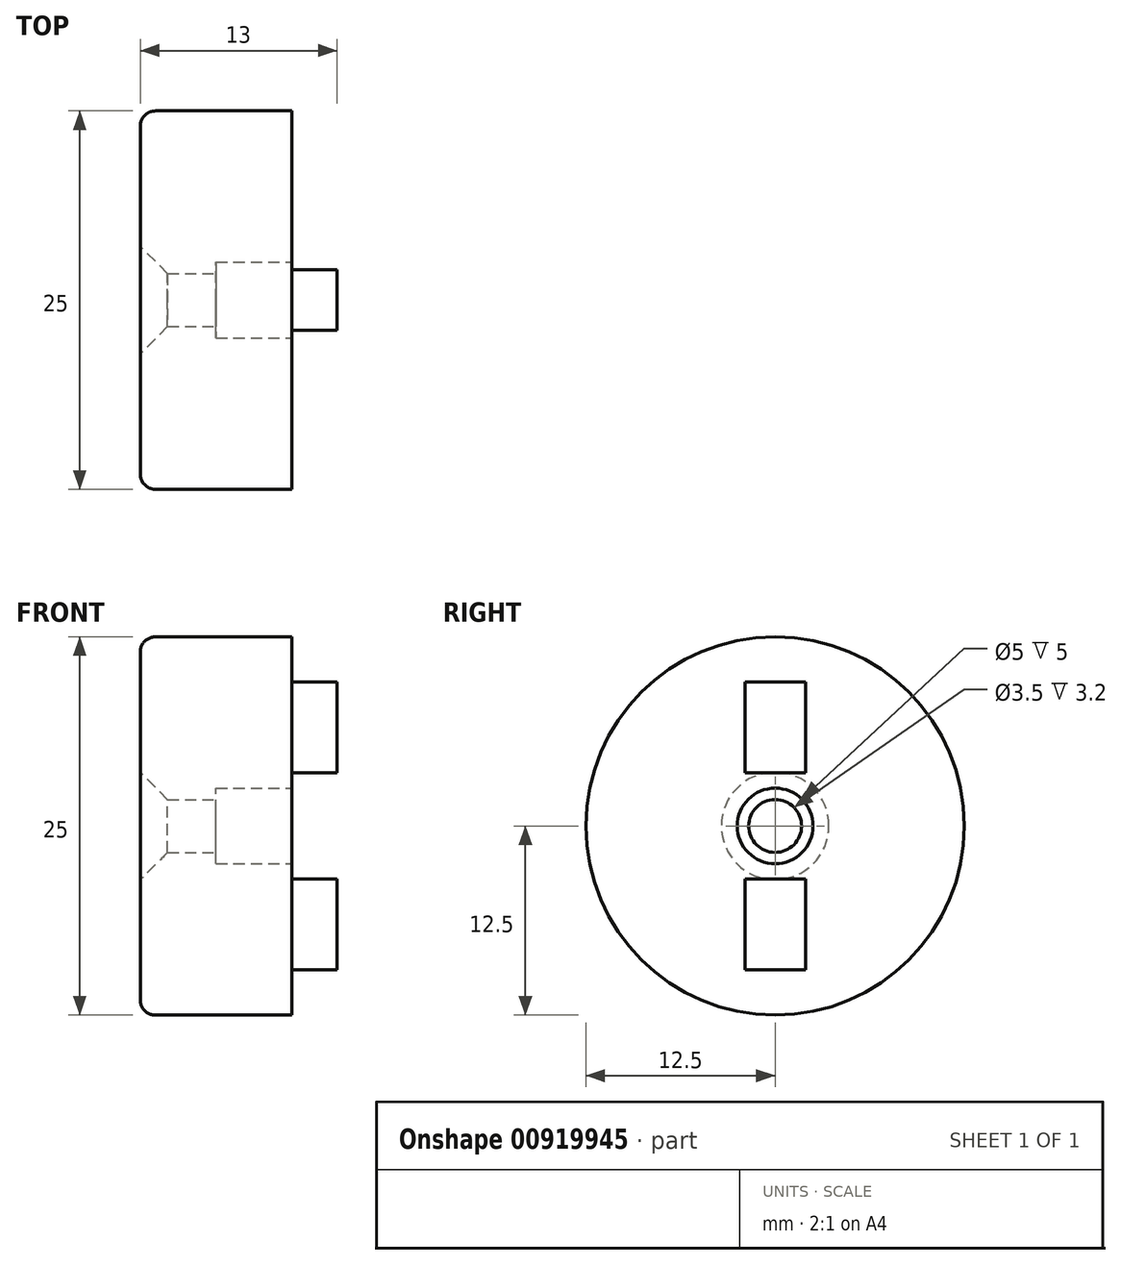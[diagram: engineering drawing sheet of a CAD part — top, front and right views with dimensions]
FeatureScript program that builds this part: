
annotation { "Feature Type Name" : "Feature", "Feature Type Description" : "" }
export const myFeature = defineFeature(function(context is Context, id is Id, definition is map)
    precondition{}
    {
        {
            var Q0;
            Q0=qCreatedBy(makeId("Front.planeOp"),FACE);
            var sketch = newSketch(context, id + "F0", { "sketchPlane" : qUnion([Q0])});
            skLineSegment(sketch, "E0", {"start": v(0, 0) * mm, "end": v(19.37, 0) * mm, "construction": true});
            skLineSegment(sketch, "E1.bottom", {"start": v(0, 0) * mm, "end": v(13, 0) * mm});
            skLineSegment(sketch, "E1.top", {"start": v(0, 12.5) * mm, "end": v(13, 12.5) * mm});
            skLineSegment(sketch, "E1.left", {"start": v(0, 0) * mm, "end": v(0, 12.5) * mm});
            skLineSegment(sketch, "E1.right", {"start": v(13, 0) * mm, "end": v(13, 12.5) * mm});
            skSolve(sketch);
        }
        {
            var Q0;
            Q0 = qSketchRegion(id + "F0", true);
            var Q1;
            Q1=sQuery(id+"F0.wireOp",EDGE,"E0");
            revolve(context, id + "F1", {"surfaceOperationType" : NewSurfaceOperationType.NEW, "entities" : qUnion([Q0]), "axis" : qUnion([Q1]), "revolveType" : RevolveType.FULL});
        }
        {
            var Q0;
            Q0=makeQuery(id+"F1.opRevolve","SWEPT_FACE",FACE,{"disambiguationData":[OSD([sQuery(id+"F0.wireOp",EDGE,"E1.right")])]});
            var sketch = newSketch(context, id + "F2", { "sketchPlane" : qUnion([Q0])});
            skLineSegment(sketch, "E2", {"start": v(0, 0) * mm, "end": v(0, 16.79) * mm, "construction": true});
            skLineSegment(sketch, "E3", {"start": v(0, 0) * mm, "end": v(18.6, 0) * mm, "construction": true});
            skLineSegment(sketch, "E4.bottom", {"start": v(-2, 9.5) * mm, "end": v(2, 9.5) * mm});
            skLineSegment(sketch, "E4.top", {"start": v(-2, 3.5) * mm, "end": v(2, 3.5) * mm});
            skLineSegment(sketch, "E4.left", {"start": v(-2, 9.5) * mm, "end": v(-2, 3.5) * mm});
            skLineSegment(sketch, "E4.right", {"start": v(2, 9.5) * mm, "end": v(2, 3.5) * mm});
            skLineSegment(sketch, "E5.MirrorCS", {"start": v(-2, -3.5) * mm, "end": v(2, -3.5) * mm});
            skLineSegment(sketch, "E6.MirrorCS", {"start": v(-2, -9.5) * mm, "end": v(-2, -3.5) * mm});
            skLineSegment(sketch, "E7.MirrorCS", {"start": v(-2, -9.5) * mm, "end": v(2, -9.5) * mm});
            skLineSegment(sketch, "E8.MirrorCS", {"start": v(2, -9.5) * mm, "end": v(2, -3.5) * mm});
            skCircle(sketch, "E9.0", {"center": v(0, 0) * mm, "radius": 12.5 * mm});
            skSolve(sketch);
        }
        {
            var Q0;
            Q0 = qSketchRegion(id + "F2", true);
            extrude(context, id + "F3", {"entities" : qUnion([Q0]), "operationType" : NewBodyOperationType.REMOVE, "oppositeDirection" : true, "depth" : 3 * mm, "offsetDistance" : 25 * mm});
        }
        {
            var Q0;
            Q0=qCreatedBy(makeId("Front.planeOp"),FACE);
            var sketch = newSketch(context, id + "F4", { "sketchPlane" : qUnion([Q0])});
            skLineSegment(sketch, "E10", {"start": v(0, 0) * mm, "end": v(15.62, 0) * mm, "construction": true});
            skLineSegment(sketch, "E11.bottom", {"start": v(5, 0) * mm, "end": v(13, 0) * mm});
            skLineSegment(sketch, "E11.top", {"start": v(5, 2.5) * mm, "end": v(13, 2.5) * mm});
            skLineSegment(sketch, "E11.left", {"start": v(5, 0) * mm, "end": v(5, 2.5) * mm});
            skLineSegment(sketch, "E11.right", {"start": v(13, 0) * mm, "end": v(13, 2.5) * mm});
            skSolve(sketch);
        }
        {
            var Q0;
            Q0 = qSketchRegion(id + "F4", true);
            var Q1;
            Q1=sQuery(id+"F4.wireOp",EDGE,"E10");
            revolve(context, id + "F5", {"operationType" : NewBodyOperationType.REMOVE, "surfaceOperationType" : NewSurfaceOperationType.NEW, "entities" : qUnion([Q0]), "axis" : qUnion([Q1]), "revolveType" : RevolveType.FULL, "oppositeDirection" : true});
        }
        {
            var Q0;
            Q0=qCreatedBy(makeId("Front.planeOp"),FACE);
            var sketch = newSketch(context, id + "F6", { "sketchPlane" : qUnion([Q0])});
            skLineSegment(sketch, "E12", {"start": v(0, 0) * mm, "end": v(11.05, 0) * mm, "construction": true});
            skLineSegment(sketch, "E13", {"start": v(0, 0) * mm, "end": v(0, 3.55) * mm});
            skLineSegment(sketch, "E14", {"start": v(0, 3.55) * mm, "end": v(1.8, 1.75) * mm});
            skLineSegment(sketch, "E15", {"start": v(1.8, 1.75) * mm, "end": v(6.23, 1.75) * mm});
            skLineSegment(sketch, "E16", {"start": v(6.23, 1.75) * mm, "end": v(6.23, 0) * mm});
            skLineSegment(sketch, "E17", {"start": v(6.23, 0) * mm, "end": v(0, 0) * mm});
            skSolve(sketch);
        }
        {
            var Q0;
            Q0 = qSketchRegion(id + "F6", true);
            var Q1;
            Q1=sQuery(id+"F6.wireOp",EDGE,"E12");
            revolve(context, id + "F7", {"operationType" : NewBodyOperationType.REMOVE, "surfaceOperationType" : NewSurfaceOperationType.NEW, "entities" : qUnion([Q0]), "axis" : qUnion([Q1]), "revolveType" : RevolveType.FULL, "oppositeDirection" : true});
        }
        {
            var Q0;
            Q0=makeQuery(id+"F3.boolean.opBoolean","COPY",EDGE,{"derivedFrom":makeQuery(id+"F3.opExtrude","CAP_EDGE",EDGE,{"disambiguationData":[OSD([sQuery(id+"F2.wireOp",EDGE,"E9.0")])],"isStart":false})});
            var Q1;
            Q1=makeQuery(id+"F1.opRevolve","SWEPT_EDGE",EDGE,{"disambiguationData":[OSD([sQuery(id+"F0.wireOp",EDGE,"E1.top"),sQuery(id+"F0.wireOp",EDGE,"E1.left")])]});
            fillet(context, id + "F8", {"entities" : qUnion([Q0, Q1]), "radius" : 1 * mm, "tangentPropagation" : true, "allowEdgeOverflow" : false});
        }
    });
